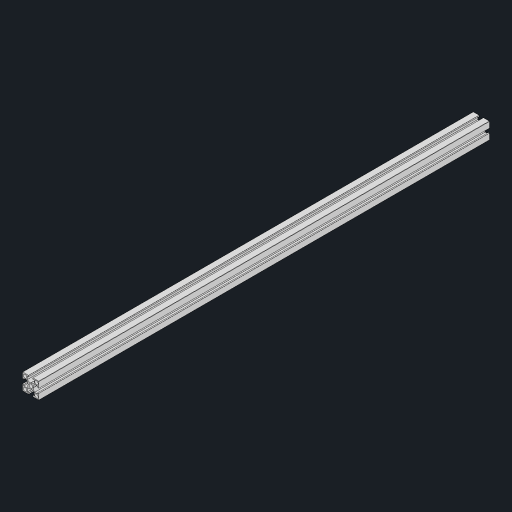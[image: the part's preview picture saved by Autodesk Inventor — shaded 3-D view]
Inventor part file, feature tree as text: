
AUTODESK INVENTOR PART (.ipt)
format: ipt  version: 2024.2 (Build 282272000, 272)  size: 231,936 bytes
history: native  units: mm
features: other x1, extrude x1, fillet x1, sketch x1
ambient origin geometry x8: Origin, YZ Plane, XZ Plane, XY Plane, X Axis, Y Axis, Z Axis, Center Point
bodies: Body1 (feature_tree)
feature tree (4):
  other  "솔리드1"
  extrude  "프로파일 길이 설정"  Depth=20.0mm
  fillet  "모서리"  Radius=20.0mm
  sketch  "스케치1"
